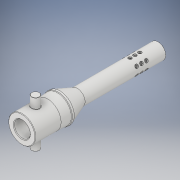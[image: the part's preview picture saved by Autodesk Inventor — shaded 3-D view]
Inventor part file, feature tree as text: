
AUTODESK INVENTOR PART (.ipt)
format: ipt  version: 2019 (Build 230136000, 136)  size: 670,208 bytes
history: native  units: mm
features: other x3, extrude x2, sketch x2, chamfer x1, mirror x1, fillet x1, pattern_circular x1
ambient origin geometry x8: Origin, YZ Plane, XZ Plane, XY Plane, X Axis, Y Axis, Z Axis, Center Point
bodies: Solide1 (feature_tree)
feature tree (11):
  other  "Révolution1"
  other  "Plan de construction2"
  extrude  "Extrusion2"  Depth=2.15mm
  chamfer  "Chanfrein1"  Distance=0.625mm
  mirror  "Symétrie1"
  other  "Plan de construction1"
  extrude  "Extrusion3"  Depth=0.625mm
  fillet  "Congé2"  Radius=0.5mm
  pattern_circular  "Réseau circulaire3"  [2 undecoded]
  sketch  "Esquisse3"
  sketch  "Esquisse5"
note: 2 required parameter values undecoded (feature->parameter linkage not recoverable at this tier; creation-order binding heuristic only, values carry confidence <= 0.55)
